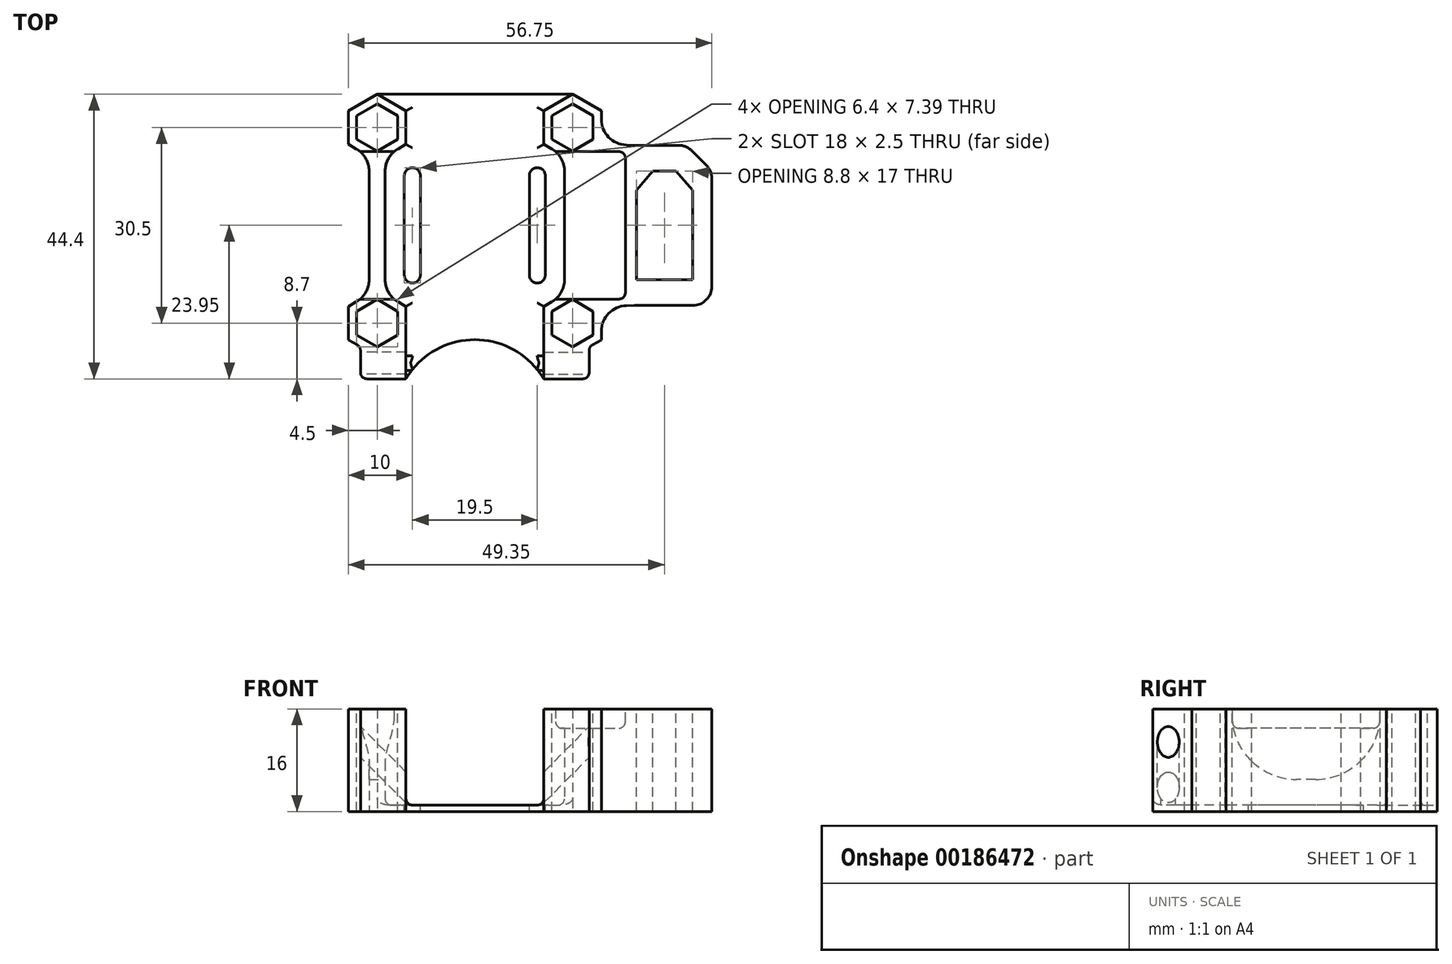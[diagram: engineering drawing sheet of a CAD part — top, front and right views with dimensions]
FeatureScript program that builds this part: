
annotation { "Feature Type Name" : "Feature", "Feature Type Description" : "" }
export const myFeature = defineFeature(function(context is Context, id is Id, definition is map)
    precondition{}
    {
        {
            var Q0;
            Q0=qCreatedBy(makeId("Top.planeOp"),FACE);
            var sketch = newSketch(context, id + "F0", { "sketchPlane" : qUnion([Q0])});
            skLineSegment(sketch, "E0.bottom", {"start": v(-15.25, 20.45) * mm, "end": v(15.25, 20.45) * mm});
            skLineSegment(sketch, "E0.top", {"start": v(-15.25, -20.45) * mm, "end": v(15.25, -20.45) * mm});
            skLineSegment(sketch, "E0.left", {"start": v(-15.25, 20.45) * mm, "end": v(-15.25, -20.45) * mm});
            skLineSegment(sketch, "E0.right", {"start": v(15.25, 20.45) * mm, "end": v(15.25, -20.45) * mm});
            skSolve(sketch);
        }
        {
            var Q0;
            Q0=qSketchRegion(id+"F0",true);
            extrude(context, id + "F1", {"entities" : qUnion([Q0]), "depth" : 1 * mm});
        }
        {
            var Q0;
            Q0=qCreatedBy(makeId("Top.planeOp"),FACE);
            var sketch = newSketch(context, id + "F2", { "sketchPlane" : qUnion([Q0])});
            skCircle(sketch, "E1.cCircle", {"center": v(-15.25, 15.25) * mm, "radius": 4.5 * mm, "construction": true});
            skLineSegment(sketch, "E1.0", {"start": v(-16.5, 10.78) * mm, "end": v(-19.75, 12.65) * mm});
            skLineSegment(sketch, "E1.1", {"start": v(-19.75, 12.65) * mm, "end": v(-19.75, 17.85) * mm});
            skLineSegment(sketch, "E1.2", {"start": v(-19.75, 17.85) * mm, "end": v(-15.25, 20.45) * mm});
            skLineSegment(sketch, "E1.3", {"start": v(-15.25, 20.45) * mm, "end": v(-10.75, 17.85) * mm});
            skLineSegment(sketch, "E1.4", {"start": v(-10.75, 17.85) * mm, "end": v(-10.75, 12.65) * mm});
            skLineSegment(sketch, "E1.5", {"start": v(-10.75, 12.65) * mm, "end": v(-14, 10.78) * mm});
            skPoint(sketch, "E1.0.midPoint", {"position": v(-17.5, 11.35) * mm});
            skCircle(sketch, "E2.MirrorC", {"center": v(15.25, 15.25) * mm, "radius": 4.5 * mm, "construction": true});
            skLineSegment(sketch, "E3.MirrorCS", {"start": v(19.75, 12.65) * mm, "end": v(19.75, 17.85) * mm});
            skLineSegment(sketch, "E4.MirrorCS", {"start": v(19.75, 17.85) * mm, "end": v(15.25, 20.45) * mm});
            skLineSegment(sketch, "E5.MirrorCS", {"start": v(15.25, 20.45) * mm, "end": v(10.75, 17.85) * mm});
            skLineSegment(sketch, "E6.MirrorCS", {"start": v(10.75, 17.85) * mm, "end": v(10.75, 12.65) * mm});
            skLineSegment(sketch, "E7.MirrorCS", {"start": v(10.75, 12.65) * mm, "end": v(14, 10.78) * mm});
            skPoint(sketch, "E8.MirrorP", {"position": v(17.5, 11.35) * mm});
            skLineSegment(sketch, "E9.MirrorCS", {"start": v(-16.5, -10.78) * mm, "end": v(-19.75, -12.65) * mm});
            skLineSegment(sketch, "E10.MirrorCS", {"start": v(-19.75, -12.65) * mm, "end": v(-19.75, -17.85) * mm});
            skLineSegment(sketch, "E11.MirrorCS", {"start": v(10.75, -17.85) * mm, "end": v(10.75, -12.65) * mm});
            skLineSegment(sketch, "E12.MirrorCS", {"start": v(10.75, -12.65) * mm, "end": v(14, -10.78) * mm});
            skLineSegment(sketch, "E13.MirrorCS", {"start": v(-19.75, -17.85) * mm, "end": v(-15.25, -20.45) * mm});
            skLineSegment(sketch, "E14.MirrorCS", {"start": v(15.25, -20.45) * mm, "end": v(10.75, -17.85) * mm});
            skLineSegment(sketch, "E15.MirrorCS", {"start": v(-15.25, -20.45) * mm, "end": v(-10.75, -17.85) * mm});
            skLineSegment(sketch, "E16.MirrorCS", {"start": v(19.75, -17.85) * mm, "end": v(15.25, -20.45) * mm});
            skLineSegment(sketch, "E17.MirrorCS", {"start": v(-10.75, -17.85) * mm, "end": v(-10.75, -12.65) * mm});
            skLineSegment(sketch, "E18.MirrorCS", {"start": v(19.75, -12.65) * mm, "end": v(19.75, -17.85) * mm});
            skCircle(sketch, "E19.MirrorC", {"center": v(-15.25, -15.25) * mm, "radius": 4.5 * mm, "construction": true});
            skCircle(sketch, "E20.MirrorC", {"center": v(15.25, -15.25) * mm, "radius": 4.5 * mm, "construction": true});
            skPoint(sketch, "E21.MirrorP", {"position": v(17.5, -11.35) * mm});
            skLineSegment(sketch, "E22.MirrorCS", {"start": v(-10.75, -12.65) * mm, "end": v(-14, -10.78) * mm});
            skPoint(sketch, "E23.MirrorP", {"position": v(-17.5, -11.35) * mm});
            skLineSegment(sketch, "E24", {"start": v(-16.5, 10.78) * mm, "end": v(-16.5, -10.78) * mm});
            skLineSegment(sketch, "E25", {"start": v(-14, -10.78) * mm, "end": v(-14, 10.78) * mm});
            skLineSegment(sketch, "E26", {"start": v(14, 10.78) * mm, "end": v(14, -10.78) * mm});
            skPoint(sketch, "E27.orphan", {"position": v(-15.25, 10.05) * mm});
            skPoint(sketch, "E28.orphan", {"position": v(-15.25, -10.05) * mm});
            skPoint(sketch, "E29.orphan", {"position": v(15.25, -10.05) * mm});
            skPoint(sketch, "E30.orphan", {"position": v(15.25, 10.05) * mm});
            skLineSegment(sketch, "E31", {"start": v(25, 12.5) * mm, "end": v(25, -12.5) * mm, "construction": true});
            skLineSegment(sketch, "E32", {"start": v(25, -12.5) * mm, "end": v(19.75, -12.65) * mm});
            skLineSegment(sketch, "E33", {"start": v(25, 12.5) * mm, "end": v(19.75, 12.65) * mm});
            skLineSegment(sketch, "E34.bottom", {"start": v(25, 12.5) * mm, "end": v(37, 12.5) * mm});
            skLineSegment(sketch, "E34.top", {"start": v(24, -12.5) * mm, "end": v(37, -12.5) * mm});
            skLineSegment(sketch, "E34.right", {"start": v(37, 12.5) * mm, "end": v(37, -12.5) * mm});
            skSolve(sketch);
        }
        {
            var Q0;
            Q0=qSketchRegion(id+"F2",true);
            extrude(context, id + "F3", {"entities" : qUnion([Q0]), "operationType" : NewBodyOperationType.ADD, "depth" : 16 * mm});
        }
        {
            var Q0;
            Q0=makeQuery(id+"F3.opExtrude","CAP_FACE",FACE,{"disambiguationData":[OSD([sQuery(id+"F2.wireOp",EDGE,"E3.MirrorCS"),sQuery(id+"F2.wireOp",EDGE,"E4.MirrorCS"),sQuery(id+"F2.wireOp",EDGE,"E5.MirrorCS"),sQuery(id+"F2.wireOp",EDGE,"E6.MirrorCS"),sQuery(id+"F2.wireOp",EDGE,"E7.MirrorCS"),sQuery(id+"F2.wireOp",EDGE,"E11.MirrorCS"),sQuery(id+"F2.wireOp",EDGE,"E12.MirrorCS"),sQuery(id+"F2.wireOp",EDGE,"E14.MirrorCS"),sQuery(id+"F2.wireOp",EDGE,"E16.MirrorCS"),sQuery(id+"F2.wireOp",EDGE,"E18.MirrorCS"),sQuery(id+"F2.wireOp",EDGE,"E26"),sQuery(id+"F2.wireOp",EDGE,"E31"),sQuery(id+"F2.wireOp",EDGE,"E32"),sQuery(id+"F2.wireOp",EDGE,"E33")])],"isStart":false});
            var sketch = newSketch(context, id + "F4", { "sketchPlane" : qUnion([Q0])});
            skLineSegment(sketch, "E35.bottom", {"start": v(-24.5, 11.5) * mm, "end": v(23.5, 11.5) * mm});
            skLineSegment(sketch, "E35.top", {"start": v(-24.5, -11.5) * mm, "end": v(23.5, -11.5) * mm});
            skLineSegment(sketch, "E35.left", {"start": v(-24.5, 11.5) * mm, "end": v(-24.5, -11.5) * mm});
            skLineSegment(sketch, "E35.right", {"start": v(23.5, 11.5) * mm, "end": v(23.5, -11.5) * mm});
            skPoint(sketch, "E36.visualSharp", {"position": v(23.5, 11.5) * mm});
            skPoint(sketch, "E37.visualSharp", {"position": v(23.5, -11.5) * mm});
            skSolve(sketch);
        }
        {
            var Q0;
            Q0=qSketchRegion(id+"F4",true);
            extrude(context, id + "F5", {"entities" : qUnion([Q0]), "operationType" : NewBodyOperationType.REMOVE, "oppositeDirection" : true, "depth" : 3 * mm});
        }
        {
            var Q0;
            {var subQ0=sQuery(id+"F2.wireOp",EDGE,"E34.top");var subQ1=sQuery(id+"F2.wireOp",EDGE,"E34.bottom");var subQ2=sQuery(id+"F2.wireOp",EDGE,"E33");var subQ3=sQuery(id+"F2.wireOp",EDGE,"E32");var subQ4=sQuery(id+"F2.wireOp",EDGE,"E34.right");Q0=makeQuery(id+"F5.boolean.opBoolean","SPLIT",FACE,{"disambiguationData":[TD([makeQuery(id+"F3.opExtrude","SWEPT_FACE",FACE,{"disambiguationData":[OSD([subQ3])]})])],"derivedFrom":makeQuery(id+"F3.opExtrude","CAP_FACE",FACE,{"disambiguationData":[OSD([sQuery(id+"F2.wireOp",EDGE,"E3.MirrorCS"),sQuery(id+"F2.wireOp",EDGE,"E4.MirrorCS"),sQuery(id+"F2.wireOp",EDGE,"E5.MirrorCS"),sQuery(id+"F2.wireOp",EDGE,"E6.MirrorCS"),sQuery(id+"F2.wireOp",EDGE,"E7.MirrorCS"),sQuery(id+"F2.wireOp",EDGE,"E11.MirrorCS"),sQuery(id+"F2.wireOp",EDGE,"E12.MirrorCS"),sQuery(id+"F2.wireOp",EDGE,"E14.MirrorCS"),sQuery(id+"F2.wireOp",EDGE,"E16.MirrorCS"),sQuery(id+"F2.wireOp",EDGE,"E18.MirrorCS"),sQuery(id+"F2.wireOp",EDGE,"E26"),subQ3,subQ2,subQ1,subQ0,subQ4])],"isStart":false})});}
            var sketch = newSketch(context, id + "F6", { "sketchPlane" : qUnion([Q0])});
            skLineSegment(sketch, "E38.bottom", {"start": v(27.8, 8.5) * mm, "end": v(31.4, 8.5) * mm});
            skLineSegment(sketch, "E38.top", {"start": v(25.2, -8.5) * mm, "end": v(34, -8.5) * mm});
            skLineSegment(sketch, "E38.left", {"start": v(25.2, 5.5) * mm, "end": v(25.2, -8.5) * mm});
            skLineSegment(sketch, "E38.right", {"start": v(34, 5.5) * mm, "end": v(34, -8.5) * mm});
            skLineSegment(sketch, "E39", {"start": v(27.8, 8.5) * mm, "end": v(25.2, 5.5) * mm});
            skLineSegment(sketch, "E40", {"start": v(31.4, 8.5) * mm, "end": v(34, 5.5) * mm});
            skCircle(sketch, "E41.cCircle", {"center": v(-15.25, 15.25) * mm, "radius": 3.2 * mm, "construction": true});
            skLineSegment(sketch, "E41.0", {"start": v(-12.05, 13.4) * mm, "end": v(-15.25, 11.55) * mm});
            skLineSegment(sketch, "E41.1", {"start": v(-15.25, 11.55) * mm, "end": v(-18.45, 13.4) * mm});
            skLineSegment(sketch, "E41.2", {"start": v(-18.45, 13.4) * mm, "end": v(-18.45, 17.1) * mm});
            skLineSegment(sketch, "E41.3", {"start": v(-18.45, 17.1) * mm, "end": v(-15.25, 18.95) * mm});
            skLineSegment(sketch, "E41.4", {"start": v(-15.25, 18.95) * mm, "end": v(-12.05, 17.1) * mm});
            skLineSegment(sketch, "E41.5", {"start": v(-12.05, 17.1) * mm, "end": v(-12.05, 13.4) * mm});
            skPoint(sketch, "E41.0.midPoint", {"position": v(-13.65, 12.48) * mm});
            skLineSegment(sketch, "E42.0.1.0", {"start": v(-15.25, -11.55) * mm, "end": v(-12.05, -13.4) * mm});
            skLineSegment(sketch, "E42.0.1.1", {"start": v(-15.25, -18.95) * mm, "end": v(-18.45, -17.1) * mm});
            skLineSegment(sketch, "E42.0.1.2", {"start": v(-18.45, -13.4) * mm, "end": v(-15.25, -11.55) * mm});
            skPoint(sketch, "E42.0.1.3", {"position": v(-13.65, -18.02) * mm});
            skCircle(sketch, "E42.0.1.4", {"center": v(-15.25, -15.25) * mm, "radius": 3.2 * mm, "construction": true});
            skLineSegment(sketch, "E42.0.1.5", {"start": v(-12.05, -13.4) * mm, "end": v(-12.05, -17.1) * mm});
            skLineSegment(sketch, "E42.0.1.6", {"start": v(-18.45, -17.1) * mm, "end": v(-18.45, -13.4) * mm});
            skLineSegment(sketch, "E42.0.1.7", {"start": v(-12.05, -17.1) * mm, "end": v(-15.25, -18.95) * mm});
            skLineSegment(sketch, "E42.direction1", {"start": v(-18.45, 13.4) * mm, "end": v(12.05, 13.4) * mm, "construction": true});
            skLineSegment(sketch, "E42.direction2", {"start": v(-18.45, 13.4) * mm, "end": v(-18.45, -17.1) * mm, "construction": true});
            skLineSegment(sketch, "E43.MirrorCS", {"start": v(12.05, 17.1) * mm, "end": v(12.05, 13.4) * mm});
            skLineSegment(sketch, "E44.MirrorCS", {"start": v(18.45, 17.1) * mm, "end": v(15.25, 18.95) * mm});
            skLineSegment(sketch, "E45.MirrorCS", {"start": v(12.05, -17.1) * mm, "end": v(15.25, -18.95) * mm});
            skLineSegment(sketch, "E46.MirrorCS", {"start": v(18.45, 13.4) * mm, "end": v(18.45, 17.1) * mm});
            skLineSegment(sketch, "E47.MirrorCS", {"start": v(15.25, 11.55) * mm, "end": v(18.45, 13.4) * mm});
            skLineSegment(sketch, "E48.MirrorCS", {"start": v(12.05, 13.4) * mm, "end": v(15.25, 11.55) * mm});
            skLineSegment(sketch, "E49.MirrorCS", {"start": v(18.45, -13.4) * mm, "end": v(15.25, -11.55) * mm});
            skLineSegment(sketch, "E50.MirrorCS", {"start": v(15.25, -11.55) * mm, "end": v(12.05, -13.4) * mm});
            skLineSegment(sketch, "E51.MirrorCS", {"start": v(12.05, -13.4) * mm, "end": v(12.05, -17.1) * mm});
            skLineSegment(sketch, "E52.MirrorCS", {"start": v(18.45, -17.1) * mm, "end": v(18.45, -13.4) * mm});
            skLineSegment(sketch, "E53.MirrorCS", {"start": v(15.25, 18.95) * mm, "end": v(12.05, 17.1) * mm});
            skCircle(sketch, "E54.MirrorC", {"center": v(15.25, -15.25) * mm, "radius": 3.2 * mm, "construction": true});
            skLineSegment(sketch, "E55.MirrorCS", {"start": v(15.25, -18.95) * mm, "end": v(18.45, -17.1) * mm});
            skPoint(sketch, "E56.MirrorP", {"position": v(13.65, -18.02) * mm});
            skLineSegment(sketch, "E57.MirrorCS", {"start": v(18.45, 13.4) * mm, "end": v(18.45, -17.1) * mm, "construction": true});
            skPoint(sketch, "E58.MirrorP", {"position": v(13.65, 12.48) * mm});
            skCircle(sketch, "E59.MirrorC", {"center": v(15.25, 15.25) * mm, "radius": 3.2 * mm, "construction": true});
            skSolve(sketch);
        }
        {
            var Q0;
            Q0=makeQuery(id+"F3.opExtrude","SWEPT_EDGE",EDGE,{"disambiguationData":[OSD([sQuery(id+"F2.wireOp",EDGE,"E34.bottom"),sQuery(id+"F2.wireOp",EDGE,"E34.right")])]});
            chamfer(context, id + "F7", {"entities" : qUnion([Q0]), "width" : 4 * mm, "tangentPropagation" : true});
        }
        {
            var Q0;
            Q0=makeQuery(id+"F3.opExtrude","SWEPT_EDGE",EDGE,{"disambiguationData":[OSD([sQuery(id+"F2.wireOp",EDGE,"E1.0"),sQuery(id+"F2.wireOp",EDGE,"E24")])]});
            var Q1;
            Q1=makeQuery(id+"F3.opExtrude","SWEPT_EDGE",EDGE,{"disambiguationData":[OSD([sQuery(id+"F2.wireOp",EDGE,"E9.MirrorCS"),sQuery(id+"F2.wireOp",EDGE,"E24")])]});
            var Q2;
            Q2=makeQuery(id+"F3.opExtrude","SWEPT_EDGE",EDGE,{"disambiguationData":[OSD([sQuery(id+"F2.wireOp",EDGE,"E1.5"),sQuery(id+"F2.wireOp",EDGE,"E25")])]});
            var Q3;
            Q3=makeQuery(id+"F3.opExtrude","SWEPT_EDGE",EDGE,{"disambiguationData":[OSD([sQuery(id+"F2.wireOp",EDGE,"E22.MirrorCS"),sQuery(id+"F2.wireOp",EDGE,"E25")])]});
            var Q4;
            Q4=makeQuery(id+"F3.opExtrude","SWEPT_EDGE",EDGE,{"disambiguationData":[OSD([sQuery(id+"F2.wireOp",EDGE,"E7.MirrorCS"),sQuery(id+"F2.wireOp",EDGE,"E26")])]});
            var Q5;
            Q5=makeQuery(id+"F3.opExtrude","SWEPT_EDGE",EDGE,{"disambiguationData":[OSD([sQuery(id+"F2.wireOp",EDGE,"E12.MirrorCS"),sQuery(id+"F2.wireOp",EDGE,"E26")])]});
            var Q6;
            Q6=makeQuery(id+"F3.opExtrude","SWEPT_EDGE",EDGE,{"disambiguationData":[OSD([sQuery(id+"F2.wireOp",EDGE,"E33"),sQuery(id+"F2.wireOp",EDGE,"E34.bottom")])]});
            var Q7;
            Q7=makeQuery(id+"F3.opExtrude","SWEPT_EDGE",EDGE,{"disambiguationData":[OSD([sQuery(id+"F2.wireOp",EDGE,"E3.MirrorCS"),sQuery(id+"F2.wireOp",EDGE,"E33")])]});
            var Q8;
            Q8=makeQuery(id+"F3.opExtrude","SWEPT_EDGE",EDGE,{"disambiguationData":[OSD([sQuery(id+"F2.wireOp",EDGE,"E18.MirrorCS"),sQuery(id+"F2.wireOp",EDGE,"E32")])]});
            var Q9;
            Q9=makeQuery(id+"F3.opExtrude","SWEPT_EDGE",EDGE,{"disambiguationData":[OSD([sQuery(id+"F2.wireOp",EDGE,"E32"),sQuery(id+"F2.wireOp",EDGE,"E34.top")])]});
            fillet(context, id + "F8", {"entities" : qUnion([Q0, Q1, Q2, Q3, Q4, Q5, Q6, Q7, Q8, Q9]), "radius" : 4 * mm, "tangentPropagation" : true, "allowEdgeOverflow" : false});
        }
        {
            var Q0;
            {var subQ1=sQuery(id+"F4.wireOp",EDGE,"E35.bottom");Q0=makeQuery(id+"F5.boolean.opBoolean","COPY",EDGE,{"disambiguationData":[TD([makeQuery(id+"F3.opExtrude","SWEPT_FACE",FACE,{"disambiguationData":[OSD([sQuery(id+"F2.wireOp",EDGE,"E3.MirrorCS")])]})])],"derivedFrom":makeQuery(id+"F5.opExtrude","CAP_EDGE",EDGE,{"disambiguationData":[OSD([subQ1])],"isStart":false})});}
            var Q1;
            {var subQ0=sQuery(id+"F4.wireOp",EDGE,"E35.top");Q1=makeQuery(id+"F5.boolean.opBoolean","COPY",EDGE,{"disambiguationData":[TD([makeQuery(id+"F3.opExtrude","SWEPT_FACE",FACE,{"disambiguationData":[OSD([sQuery(id+"F2.wireOp",EDGE,"E12.MirrorCS")])]})])],"derivedFrom":makeQuery(id+"F5.opExtrude","CAP_EDGE",EDGE,{"disambiguationData":[OSD([subQ0])],"isStart":false})});}
            var Q2;
            Q2=makeQuery(id+"F5.boolean.opBoolean","COPY",EDGE,{"derivedFrom":makeQuery(id+"F5.opExtrude","CAP_EDGE",EDGE,{"disambiguationData":[OSD([sQuery(id+"F4.wireOp",EDGE,"E35.right")])],"isStart":false})});
            var Q3;
            {var subQ0=sQuery(id+"F4.wireOp",EDGE,"E35.bottom");Q3=makeQuery(id+"F5.boolean.opBoolean","COPY",EDGE,{"disambiguationData":[TD([makeQuery(id+"F3.opExtrude","SWEPT_FACE",FACE,{"disambiguationData":[OSD([sQuery(id+"F2.wireOp",EDGE,"E7.MirrorCS")])]})])],"derivedFrom":makeQuery(id+"F5.opExtrude","CAP_EDGE",EDGE,{"disambiguationData":[OSD([subQ0])],"isStart":false})});}
            fillet(context, id + "F9", {"entities" : qUnion([Q0, Q1, Q2, Q3]), "radius" : 1 * mm, "tangentPropagation" : true, "allowEdgeOverflow" : false});
        }
        {
            var Q0;
            Q0=makeQuery(id+"F5.boolean.opBoolean","COPY",EDGE,{"derivedFrom":makeQuery(id+"F5.opExtrude","SWEPT_EDGE",EDGE,{"disambiguationData":[OSD([sQuery(id+"F4.wireOp",EDGE,"E35.bottom"),sQuery(id+"F4.wireOp",EDGE,"E35.right")])]})});
            var Q1;
            Q1=makeQuery(id+"F5.boolean.opBoolean","COPY",EDGE,{"derivedFrom":makeQuery(id+"F5.opExtrude","SWEPT_EDGE",EDGE,{"disambiguationData":[OSD([sQuery(id+"F4.wireOp",EDGE,"E35.top"),sQuery(id+"F4.wireOp",EDGE,"E35.right")])]})});
            fillet(context, id + "F10", {"entities" : qUnion([Q0, Q1]), "radius" : 1 * mm, "tangentPropagation" : true, "allowEdgeOverflow" : false});
        }
        {
            var Q0;
            Q0=makeQuery(id+"F3.opExtrude","SWEPT_EDGE",EDGE,{"disambiguationData":[OSD([sQuery(id+"F2.wireOp",EDGE,"E34.top"),sQuery(id+"F2.wireOp",EDGE,"E34.right")])]});
            var Q1;
            {var subQ0=sQuery(id+"F2.wireOp",EDGE,"E34.right");Q1=makeQuery(id+"F7.opChamfer","BLEND_EDGE",EDGE,{"blendedFrom":[makeQuery(id+"F3.opExtrude","SWEPT_EDGE",EDGE,{"disambiguationData":[OSD([sQuery(id+"F2.wireOp",EDGE,"E34.bottom"),subQ0])]}),makeQuery(id+"F3.opExtrude","SWEPT_FACE",FACE,{"disambiguationData":[OSD([subQ0])]})],"blendedInto":[makeQuery(id+"F3.opExtrude","SWEPT_FACE",FACE,{"disambiguationData":[OSD([subQ0])]})]});}
            var Q2;
            {var subQ0=sQuery(id+"F2.wireOp",EDGE,"E34.bottom");Q2=makeQuery(id+"F7.opChamfer","BLEND_EDGE",EDGE,{"blendedFrom":[makeQuery(id+"F3.opExtrude","SWEPT_EDGE",EDGE,{"disambiguationData":[OSD([subQ0,sQuery(id+"F2.wireOp",EDGE,"E34.right")])]}),makeQuery(id+"F3.opExtrude","SWEPT_FACE",FACE,{"disambiguationData":[OSD([subQ0])]})],"blendedInto":[makeQuery(id+"F3.opExtrude","SWEPT_FACE",FACE,{"disambiguationData":[OSD([subQ0])]})]});}
            fillet(context, id + "F11", {"entities" : qUnion([Q0, Q1, Q2]), "radius" : 3 * mm, "tangentPropagation" : true, "allowEdgeOverflow" : false});
        }
        {
            var Q0;
            {var subQ0=sQuery(id+"F4.wireOp",EDGE,"E35.bottom");var subQ1=sQuery(id+"F4.wireOp",EDGE,"E35.left");var subQ2=sQuery(id+"F4.wireOp",EDGE,"E35.top");Q0=makeQuery(id+"F5.boolean.opBoolean","COPY",FACE,{"disambiguationData":[TD([makeQuery(id+"F3.opExtrude","SWEPT_FACE",FACE,{"disambiguationData":[OSD([sQuery(id+"F2.wireOp",EDGE,"E1.0")])]})])],"derivedFrom":makeQuery(id+"F5.opExtrude","CAP_FACE",FACE,{"disambiguationData":[OSD([subQ0,subQ2,subQ1,sQuery(id+"F4.wireOp",EDGE,"E35.right")])],"isStart":false})});}
            var sketch = newSketch(context, id + "F12", { "sketchPlane" : qUnion([Q0])});
            skLineSegment(sketch, "E60.bottom", {"start": v(-12.6, 11.5) * mm, "end": v(-17.9, 11.5) * mm});
            skLineSegment(sketch, "E60.top", {"start": v(-12.6, -11.5) * mm, "end": v(-17.9, -11.5) * mm});
            skLineSegment(sketch, "E60.left", {"start": v(-12.6, 11.5) * mm, "end": v(-12.6, -11.5) * mm});
            skLineSegment(sketch, "E60.right", {"start": v(-17.9, 11.5) * mm, "end": v(-17.9, -11.5) * mm});
            skSolve(sketch);
        }
        {
            var Q0;
            Q0=qSketchRegion(id+"F12",true);
            extrude(context, id + "F13", {"entities" : qUnion([Q0]), "operationType" : NewBodyOperationType.REMOVE, "oppositeDirection" : true, "depth" : 8 * mm});
        }
        {
            var Q0;
            Q0=makeQuery(id+"F13.boolean.opBoolean","COPY",EDGE,{"derivedFrom":makeQuery(id+"F13.opExtrude","CAP_EDGE",EDGE,{"disambiguationData":[OSD([sQuery(id+"F12.wireOp",EDGE,"E60.bottom")])],"isStart":false})});
            var Q1;
            Q1=makeQuery(id+"F13.boolean.opBoolean","COPY",EDGE,{"derivedFrom":makeQuery(id+"F13.opExtrude","CAP_EDGE",EDGE,{"disambiguationData":[OSD([sQuery(id+"F12.wireOp",EDGE,"E60.top")])],"isStart":false})});
            fillet(context, id + "F14", {"entities" : qUnion([Q0, Q1]), "radius" : 10 * mm, "tangentPropagation" : true, "allowEdgeOverflow" : false});
        }
        {
            var Q0;
            Q0=makeQuery(id+"F1.opExtrude","CAP_FACE",FACE,{"disambiguationData":[OSD([sQuery(id+"F0.wireOp",EDGE,"E0.bottom"),sQuery(id+"F0.wireOp",EDGE,"E0.top"),sQuery(id+"F0.wireOp",EDGE,"E0.left"),sQuery(id+"F0.wireOp",EDGE,"E0.right")])],"isStart":false});
            var sketch = newSketch(context, id + "F15", { "sketchPlane" : qUnion([Q0])});
            skLineSegment(sketch, "E61.bottom", {"start": v(-9.75, 9) * mm, "end": v(-9.75, 9) * mm});
            skLineSegment(sketch, "E61.top", {"start": v(-9.75, -9) * mm, "end": v(-9.75, -9) * mm});
            skLineSegment(sketch, "E61.left", {"start": v(-11, 7.75) * mm, "end": v(-11, -7.75) * mm});
            skLineSegment(sketch, "E61.right", {"start": v(-8.5, 7.75) * mm, "end": v(-8.5, -7.75) * mm});
            skPoint(sketch, "E62.visualSharp", {"position": v(-11, 9) * mm});
            skArc(sketch, "E62.filletArc", {"start": v(-9.75, 9) * mm, "mid": v(-10.63, 8.63) * mm, "end": v(-11, 7.75) * mm});
            skPoint(sketch, "E63.visualSharp", {"position": v(-8.5, 9) * mm});
            skArc(sketch, "E63.filletArc", {"start": v(-8.5, 7.75) * mm, "mid": v(-8.87, 8.63) * mm, "end": v(-9.75, 9) * mm});
            skPoint(sketch, "E64.visualSharp", {"position": v(-11, -9) * mm});
            skArc(sketch, "E64.filletArc", {"start": v(-11, -7.75) * mm, "mid": v(-10.63, -8.63) * mm, "end": v(-9.75, -9) * mm});
            skPoint(sketch, "E65.visualSharp", {"position": v(-8.5, -9) * mm});
            skArc(sketch, "E65.filletArc", {"start": v(-9.75, -9) * mm, "mid": v(-8.87, -8.63) * mm, "end": v(-8.5, -7.75) * mm});
            skArc(sketch, "E66.MirrorCS", {"start": v(9.75, 9) * mm, "mid": v(10.63, 8.63) * mm, "end": v(11, 7.75) * mm});
            skArc(sketch, "E67.MirrorCS", {"start": v(8.5, 7.75) * mm, "mid": v(8.87, 8.63) * mm, "end": v(9.75, 9) * mm});
            skArc(sketch, "E68.MirrorCS", {"start": v(11, -7.75) * mm, "mid": v(10.63, -8.63) * mm, "end": v(9.75, -9) * mm});
            skArc(sketch, "E69.MirrorCS", {"start": v(9.75, -9) * mm, "mid": v(8.87, -8.63) * mm, "end": v(8.5, -7.75) * mm});
            skPoint(sketch, "E70.MirrorP", {"position": v(11, -9) * mm});
            skPoint(sketch, "E71.MirrorP", {"position": v(8.5, 9) * mm});
            skPoint(sketch, "E72.MirrorP", {"position": v(8.5, -9) * mm});
            skLineSegment(sketch, "E73.MirrorCS", {"start": v(8.5, 7.75) * mm, "end": v(8.5, -7.75) * mm});
            skLineSegment(sketch, "E74.MirrorCS", {"start": v(11, 7.75) * mm, "end": v(11, -7.75) * mm});
            skPoint(sketch, "E75.MirrorP", {"position": v(11, 9) * mm});
            skLineSegment(sketch, "E76.MirrorCS", {"start": v(9.75, 9) * mm, "end": v(9.75, 9) * mm});
            skLineSegment(sketch, "E77.MirrorCS", {"start": v(9.75, -9) * mm, "end": v(9.75, -9) * mm});
            skSolve(sketch);
        }
        {
            var Q0;
            Q0=qSketchRegion(id+"F15",true);
            extrude(context, id + "F16", {"entities" : qUnion([Q0]), "operationType" : NewBodyOperationType.REMOVE, "endBound" : BoundingType.THROUGH_ALL, "oppositeDirection" : true, "depth" : 25 * mm});
        }
        {
            var Q0;
            Q0=makeQuery(id+"F1.opExtrude","SWEPT_FACE",FACE,{"disambiguationData":[OSD([sQuery(id+"F0.wireOp",EDGE,"E0.top")])]});
            var sketch = newSketch(context, id + "F17", { "sketchPlane" : qUnion([Q0])});
            skLineSegment(sketch, "E78.bottom", {"start": v(-17.85, 16) * mm, "end": v(17.85, 16) * mm});
            skLineSegment(sketch, "E78.top", {"start": v(-17.85, 0) * mm, "end": v(17.85, 0) * mm});
            skLineSegment(sketch, "E78.left", {"start": v(-17.85, 16) * mm, "end": v(-17.85, 0) * mm});
            skLineSegment(sketch, "E78.right", {"start": v(17.85, 16) * mm, "end": v(17.85, 0) * mm});
            skSolve(sketch);
        }
        {
            var Q0;
            Q0 = qSketchRegion(id + "F17", true);
            extrude(context, id + "F18", {"entities" : qUnion([Q0]), "operationType" : NewBodyOperationType.ADD, "depth" : 3.5 * mm, "hasSecondDirection" : true, "secondDirectionOppositeDirection" : true, "secondDirectionDepth" : 2.6 * mm});
        }
        {
            var Q0;
            Q0=makeQuery(id+"F18.opExtrude","CAP_FACE",FACE,{"disambiguationData":[OSD([sQuery(id+"F17.wireOp",EDGE,"E78.bottom"),sQuery(id+"F17.wireOp",EDGE,"E78.top"),sQuery(id+"F17.wireOp",EDGE,"E78.left"),sQuery(id+"F17.wireOp",EDGE,"E78.right")])],"isStart":false});
            var sketch = newSketch(context, id + "F19", { "sketchPlane" : qUnion([Q0])});
            skLineSegment(sketch, "E79", {"start": v(-23, 16) * mm, "end": v(0, -7) * mm, "construction": true});
            skLineSegment(sketch, "E80", {"start": v(0, -7) * mm, "end": v(23, 16) * mm, "construction": true});
            skLineSegment(sketch, "E81", {"start": v(-10.75, 16) * mm, "end": v(-10.75, 0) * mm});
            skLineSegment(sketch, "E82", {"start": v(-10.75, 0) * mm, "end": v(10.75, 0) * mm});
            skLineSegment(sketch, "E83", {"start": v(10.75, 0) * mm, "end": v(10.75, 16) * mm});
            skLineSegment(sketch, "E84", {"start": v(10.75, 16) * mm, "end": v(-10.75, 16) * mm});
            skSolve(sketch);
        }
        {
            var Q0;
            Q0 = qSketchRegion(id + "F6", true);
            extrude(context, id + "F20", {"entities" : qUnion([Q0]), "operationType" : NewBodyOperationType.REMOVE, "oppositeDirection" : true, "depth" : 25 * mm});
        }
        {
            var Q0;
            Q0 = qSketchRegion(id + "F19", true);
            var Q1;
            Q1=makeQuery(id+"F18.opExtrude","CAP_FACE",FACE,{"disambiguationData":[OSD([sQuery(id+"F17.wireOp",EDGE,"E78.bottom"),sQuery(id+"F17.wireOp",EDGE,"E78.top"),sQuery(id+"F17.wireOp",EDGE,"E78.left"),sQuery(id+"F17.wireOp",EDGE,"E78.right")])],"isStart":true});
            extrude(context, id + "F21", {"entities" : qUnion([Q0]), "operationType" : NewBodyOperationType.REMOVE, "endBound" : BoundingType.UP_TO_SURFACE, "oppositeDirection" : true, "endBoundEntityFace" : qUnion([Q1]), "depth" : 25 * mm});
        }
        {
            var Q0;
            Q0=qCreatedBy(makeId("Front.planeOp"),FACE);
            cPlane(context, id + "F22", {"entities" : qUnion([Q0]), "cplaneType" : CPlaneType.OFFSET, "offset" : 21.5 * mm, "width" : 150 * mm, "height" : 150 * mm});
        }
        {
            var Q0;
            Q0=qCreatedBy(id+"F22.planeOp",FACE);
            var sketch = newSketch(context, id + "F23", { "sketchPlane" : qUnion([Q0])});
            skLineSegment(sketch, "E85", {"start": v(0, -7) * mm, "end": v(-23, 16) * mm, "construction": true});
            skLineSegment(sketch, "E86", {"start": v(0, -7) * mm, "end": v(23, 16) * mm, "construction": true});
            skLineSegment(sketch, "E87", {"start": v(-23, 16) * mm, "end": v(-24.2, 14.8) * mm});
            skLineSegment(sketch, "E88", {"start": v(-24.2, 14.8) * mm, "end": v(-7.23, -2.17) * mm});
            skLineSegment(sketch, "E89", {"start": v(-7.23, -2.17) * mm, "end": v(-6.03, -0.97) * mm});
            skLineSegment(sketch, "E90", {"start": v(-6.03, -0.97) * mm, "end": v(-23, 16) * mm});
            skLineSegment(sketch, "E91", {"start": v(23, 16) * mm, "end": v(24.2, 14.8) * mm});
            skLineSegment(sketch, "E92", {"start": v(6.03, -0.97) * mm, "end": v(23, 16) * mm});
            skLineSegment(sketch, "E93", {"start": v(6.03, -0.97) * mm, "end": v(7.23, -2.17) * mm});
            skLineSegment(sketch, "E94", {"start": v(7.23, -2.17) * mm, "end": v(24.2, 14.8) * mm});
            skSolve(sketch);
        }
        {
            var Q0;
            Q0=makeQuery(id+"F23.imprint","IMPRINT",FACE,{"disambiguationData":[TD([[makeQuery(id+"F23.imprint","IMPRINT",EDGE,{"derivedFrom":sQuery(id+"F23.wireOp",EDGE,"E87")}),1.0]])]});
            var Q1;
            Q1=sQuery(id+"F23.wireOp",EDGE,"E85");
            revolve(context, id + "F24", {"operationType" : NewBodyOperationType.REMOVE, "entities" : qUnion([Q0]), "axis" : qUnion([Q1]), "revolveType" : RevolveType.FULL, "oppositeDirection" : true});
        }
        {
            var Q0;
            Q0=makeQuery(id+"F23.imprint","IMPRINT",FACE,{"disambiguationData":[TD([[makeQuery(id+"F23.imprint","IMPRINT",EDGE,{"derivedFrom":sQuery(id+"F23.wireOp",EDGE,"E91")}),-1.0]])]});
            var Q1;
            Q1=sQuery(id+"F23.wireOp",EDGE,"E86");
            revolve(context, id + "F25", {"operationType" : NewBodyOperationType.REMOVE, "entities" : qUnion([Q0]), "axis" : qUnion([Q1]), "revolveType" : RevolveType.FULL, "oppositeDirection" : true});
        }
        {
            var Q0;
            Q0=makeQuery(id+"F21.boolean.opBoolean","COPY",EDGE,{"derivedFrom":makeQuery(id+"F21.opExtrude","CAP_EDGE",EDGE,{"disambiguationData":[OSD([sQuery(id+"F19.wireOp",EDGE,"E83")])],"isStart":false})});
            var Q1;
            Q1=makeQuery(id+"F21.boolean.opBoolean","COPY",EDGE,{"derivedFrom":makeQuery(id+"F21.opExtrude","CAP_EDGE",EDGE,{"disambiguationData":[OSD([sQuery(id+"F19.wireOp",EDGE,"E81")])],"isStart":false})});
            fillet(context, id + "F26", {"entities" : qUnion([Q0, Q1]), "radius" : 12.5 * mm, "tangentPropagation" : true, "allowEdgeOverflow" : false});
        }
        {
            var Q0;
            Q0=makeQuery(id+"F3.boolean.opBoolean","INTERSECT",EDGE,{"derivedFrom":[makeQuery(id+"F1.opExtrude","CAP_FACE",FACE,{"disambiguationData":[OSD([sQuery(id+"F0.wireOp",EDGE,"E0.bottom"),sQuery(id+"F0.wireOp",EDGE,"E0.top"),sQuery(id+"F0.wireOp",EDGE,"E0.left"),sQuery(id+"F0.wireOp",EDGE,"E0.right")])],"isStart":false}),makeQuery(id+"F3.opExtrude","SWEPT_FACE",FACE,{"disambiguationData":[OSD([sQuery(id+"F2.wireOp",EDGE,"E17.MirrorCS")])]})]});
            var Q1;
            Q1=makeQuery(id+"F8.opFillet","BLEND_EDGE",EDGE,{"blendedFrom":[makeQuery(id+"F3.opExtrude","SWEPT_EDGE",EDGE,{"disambiguationData":[OSD([sQuery(id+"F2.wireOp",EDGE,"E22.MirrorCS"),sQuery(id+"F2.wireOp",EDGE,"E25")])]}),makeQuery(id+"F1.opExtrude","CAP_FACE",FACE,{"disambiguationData":[OSD([sQuery(id+"F0.wireOp",EDGE,"E0.bottom"),sQuery(id+"F0.wireOp",EDGE,"E0.top"),sQuery(id+"F0.wireOp",EDGE,"E0.left"),sQuery(id+"F0.wireOp",EDGE,"E0.right")])],"isStart":false})],"blendedInto":[makeQuery(id+"F1.opExtrude","CAP_FACE",FACE,{"disambiguationData":[OSD([sQuery(id+"F0.wireOp",EDGE,"E0.bottom"),sQuery(id+"F0.wireOp",EDGE,"E0.top"),sQuery(id+"F0.wireOp",EDGE,"E0.left"),sQuery(id+"F0.wireOp",EDGE,"E0.right")])],"isStart":false})]});
            var Q2;
            Q2=makeQuery(id+"F3.boolean.opBoolean","INTERSECT",EDGE,{"derivedFrom":[makeQuery(id+"F1.opExtrude","CAP_FACE",FACE,{"disambiguationData":[OSD([sQuery(id+"F0.wireOp",EDGE,"E0.bottom"),sQuery(id+"F0.wireOp",EDGE,"E0.top"),sQuery(id+"F0.wireOp",EDGE,"E0.left"),sQuery(id+"F0.wireOp",EDGE,"E0.right")])],"isStart":false}),makeQuery(id+"F3.opExtrude","SWEPT_FACE",FACE,{"disambiguationData":[OSD([sQuery(id+"F2.wireOp",EDGE,"E1.4")])]})]});
            var Q3;
            Q3=makeQuery(id+"F3.boolean.opBoolean","INTERSECT",EDGE,{"derivedFrom":[makeQuery(id+"F1.opExtrude","CAP_FACE",FACE,{"disambiguationData":[OSD([sQuery(id+"F0.wireOp",EDGE,"E0.bottom"),sQuery(id+"F0.wireOp",EDGE,"E0.top"),sQuery(id+"F0.wireOp",EDGE,"E0.left"),sQuery(id+"F0.wireOp",EDGE,"E0.right")])],"isStart":false}),makeQuery(id+"F3.opExtrude","SWEPT_FACE",FACE,{"disambiguationData":[OSD([sQuery(id+"F2.wireOp",EDGE,"E1.3")])]})]});
            var Q4;
            Q4=makeQuery(id+"F3.boolean.opBoolean","INTERSECT",EDGE,{"derivedFrom":[makeQuery(id+"F1.opExtrude","CAP_FACE",FACE,{"disambiguationData":[OSD([sQuery(id+"F0.wireOp",EDGE,"E0.bottom"),sQuery(id+"F0.wireOp",EDGE,"E0.top"),sQuery(id+"F0.wireOp",EDGE,"E0.left"),sQuery(id+"F0.wireOp",EDGE,"E0.right")])],"isStart":false}),makeQuery(id+"F3.opExtrude","SWEPT_FACE",FACE,{"disambiguationData":[OSD([sQuery(id+"F2.wireOp",EDGE,"E11.MirrorCS")])]})]});
            var Q5;
            Q5=makeQuery(id+"F3.boolean.opBoolean","INTERSECT",EDGE,{"derivedFrom":[makeQuery(id+"F1.opExtrude","CAP_FACE",FACE,{"disambiguationData":[OSD([sQuery(id+"F0.wireOp",EDGE,"E0.bottom"),sQuery(id+"F0.wireOp",EDGE,"E0.top"),sQuery(id+"F0.wireOp",EDGE,"E0.left"),sQuery(id+"F0.wireOp",EDGE,"E0.right")])],"isStart":false}),makeQuery(id+"F3.opExtrude","SWEPT_FACE",FACE,{"disambiguationData":[OSD([sQuery(id+"F2.wireOp",EDGE,"E26")])]})]});
            var Q6;
            Q6=makeQuery(id+"F3.boolean.opBoolean","INTERSECT",EDGE,{"derivedFrom":[makeQuery(id+"F1.opExtrude","CAP_FACE",FACE,{"disambiguationData":[OSD([sQuery(id+"F0.wireOp",EDGE,"E0.bottom"),sQuery(id+"F0.wireOp",EDGE,"E0.top"),sQuery(id+"F0.wireOp",EDGE,"E0.left"),sQuery(id+"F0.wireOp",EDGE,"E0.right")])],"isStart":false}),makeQuery(id+"F3.opExtrude","SWEPT_FACE",FACE,{"disambiguationData":[OSD([sQuery(id+"F2.wireOp",EDGE,"E6.MirrorCS")])]})]});
            var Q7;
            Q7=makeQuery(id+"F3.boolean.opBoolean","INTERSECT",EDGE,{"derivedFrom":[makeQuery(id+"F1.opExtrude","CAP_FACE",FACE,{"disambiguationData":[OSD([sQuery(id+"F0.wireOp",EDGE,"E0.bottom"),sQuery(id+"F0.wireOp",EDGE,"E0.top"),sQuery(id+"F0.wireOp",EDGE,"E0.left"),sQuery(id+"F0.wireOp",EDGE,"E0.right")])],"isStart":false}),makeQuery(id+"F3.opExtrude","SWEPT_FACE",FACE,{"disambiguationData":[OSD([sQuery(id+"F2.wireOp",EDGE,"E5.MirrorCS")])]})]});
            fillet(context, id + "F27", {"entities" : qUnion([Q0, Q1, Q2, Q3, Q4, Q5, Q6, Q7]), "radius" : 1 * mm, "tangentPropagation" : true, "allowEdgeOverflow" : false});
        }
        {
            var Q0;
            Q0=makeQuery(id+"F18.opExtrude","CAP_EDGE",EDGE,{"disambiguationData":[OSD([sQuery(id+"F17.wireOp",EDGE,"E78.left")])],"isStart":false});
            var Q1;
            Q1=makeQuery(id+"F18.opExtrude","CAP_EDGE",EDGE,{"disambiguationData":[OSD([sQuery(id+"F17.wireOp",EDGE,"E78.right")])],"isStart":false});
            var Q2;
            Q2=makeQuery(id+"F18.boolean.opBoolean","INTERSECT",EDGE,{"derivedFrom":[makeQuery(id+"F3.opExtrude","SWEPT_FACE",FACE,{"disambiguationData":[OSD([sQuery(id+"F2.wireOp",EDGE,"E13.MirrorCS")])]}),makeQuery(id+"F18.opExtrude","SWEPT_FACE",FACE,{"disambiguationData":[OSD([sQuery(id+"F17.wireOp",EDGE,"E78.left")])]})]});
            var Q3;
            Q3=makeQuery(id+"F18.boolean.opBoolean","INTERSECT",EDGE,{"derivedFrom":[makeQuery(id+"F3.opExtrude","SWEPT_FACE",FACE,{"disambiguationData":[OSD([sQuery(id+"F2.wireOp",EDGE,"E16.MirrorCS")])]}),makeQuery(id+"F18.opExtrude","SWEPT_FACE",FACE,{"disambiguationData":[OSD([sQuery(id+"F17.wireOp",EDGE,"E78.right")])]})]});
            fillet(context, id + "F28", {"entities" : qUnion([Q0, Q1, Q2, Q3]), "radius" : 1 * mm, "tangentPropagation" : true, "allowEdgeOverflow" : false});
        }
    });
